# Revit family: PLIN 6.1
name_source: partatom
category: Lighting Fixtures
units: mm (PartAtom-declared; Revit-internal decimal feet)

## family parameters
Always vertical = No
Cut with Voids When Loaded = No
Light Source = No
OmniClass Number = 23.80.70.00
OmniClass Title = Lighting
Part Type = Normal
Room Calculation Point = Yes
Round Connector Dimension = Use Diameter
Shared = No
Work Plane-Based = Yes

## types (1)
- PLIN 6.1 A (3000K 14W 230Vac)
    Apparent Load Phase 1 = 5 W
    Body = L&L_Anticorodal aluminium
    CRI = CRI 80
    Code = -
    Control system = 0/1-10V, ON/OFF, DALI
    Cutout dimensions = -
    Default Elevation = 1219 mm
    Delivered lumen output = 1160 lm (3000K)
    Description = Bollards for outdoor applications
    Energy efficiency class = A A+ A++
    Features = -
    Height mm = 585 mm  [stored 1.91929 ft]
    Horizontal rotation max = 0.00°
    IP = IP65
    LED Colour = 2000K, 3000K, 4000K
    Length mm = 155 mm  [stored 0.50853 ft]
    Lens = L&L_Tempered extra-clear glass
    Lumen output at source = 1560 lm (3000K)
    Manufacturer = L&L Luce&Light
    Material = Head in aluminium, column in AISI 316L stainless steel. Screen in serigraphed, acid-etched, tempered extra-clear glass
    Model = Plin 6.1
    Mounting = surface mounted (floor)
    No. and type of led = 8 power LEDs, 2-step MacAdam, 60 000h L90 B10 (Ta 25°C)
    Notes = Non-standard heights available on request
    Optics = asymmetrical circular
    Power = 14W
    Power cables = -
    Power supply = 230Vac
    Power supply unit = built-in
not included
built-in
    URL = https://www.lucelight.it
    URL Accessories and power supply units = https://www.lucelight.it
    URL Catalogue = -
    URL DXF = https://www.lucelight.it
    URL Description = https://www.lucelight.it
    URL General code = https://www.lucelight.it
    URL IES Photometric file = https://www.lucelight.it
    URL Image = https://www.lucelight.it
    URL Technical sheet = -
    Vertical rotation max = 0.00°
    Weight kg = 2.50 kg
    Width mm = 155 mm  [stored 0.50853 ft]
    Wiring = -

note: [stored X ft] marks values corroborated as IEEE doubles in the binary element streams (Revit-internal decimal feet)

## geometry (parser evidence)
native form markers: Blend x2, Sweep x6
no freeform markers — native parametric forms only
